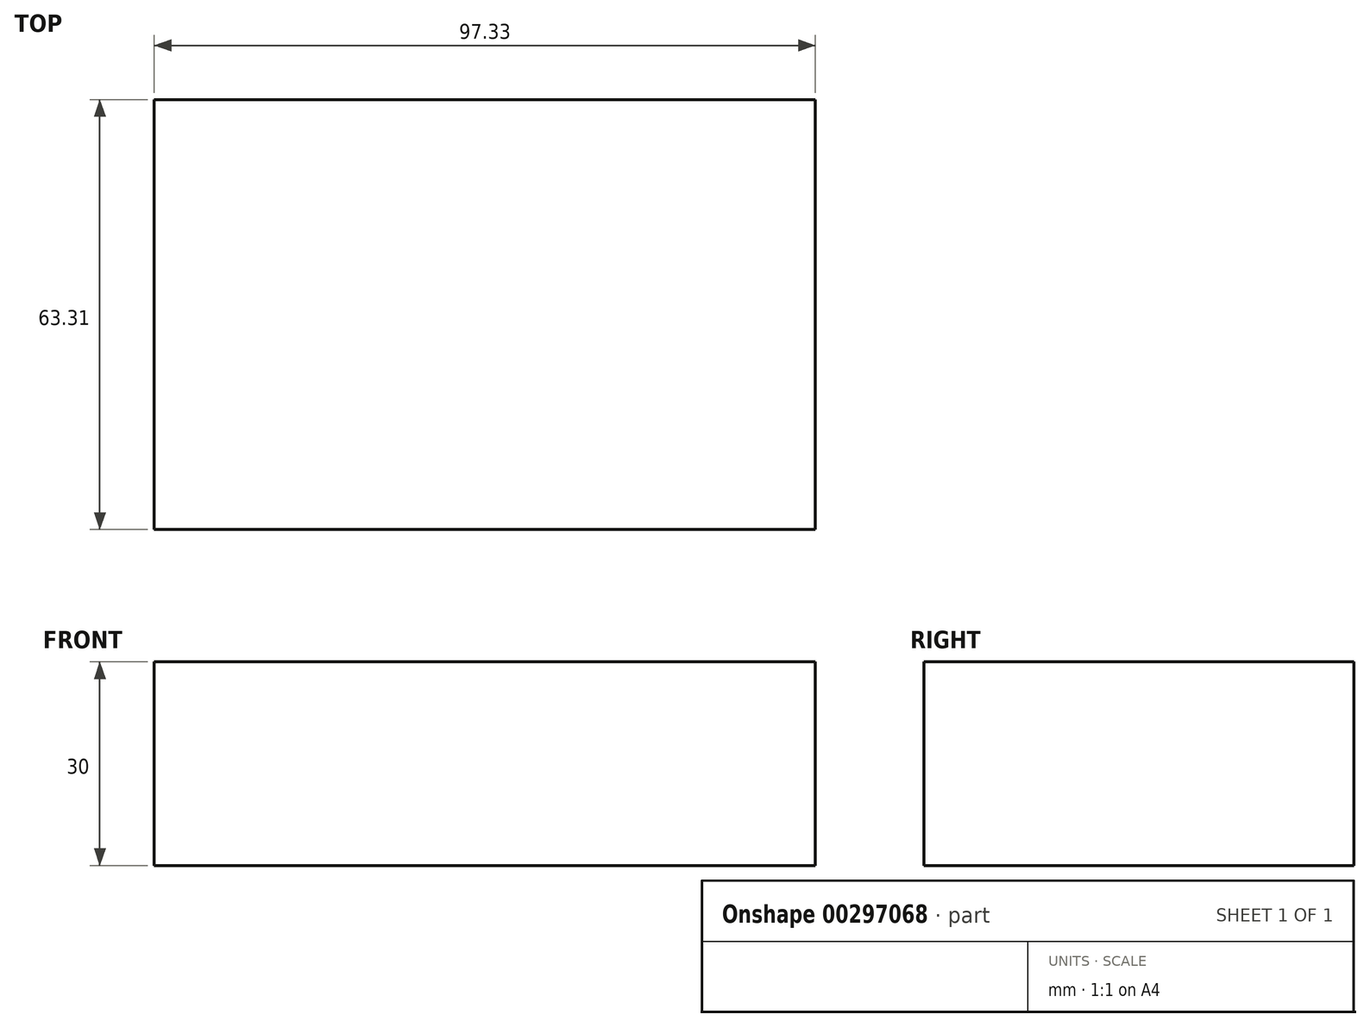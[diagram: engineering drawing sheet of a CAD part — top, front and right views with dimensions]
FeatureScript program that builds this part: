
annotation { "Feature Type Name" : "Feature", "Feature Type Description" : "" }
export const myFeature = defineFeature(function(context is Context, id is Id, definition is map)
    precondition{}
    {
        {
            var Q0;
            Q0=qCreatedBy(makeId("Top.planeOp"),FACE);
            var sketch = newSketch(context, id + "F0", { "sketchPlane" : qUnion([Q0])});
            skLineSegment(sketch, "E0.bottom", {"start": v(-44.73, 31.81) * mm, "end": v(52.6, 31.81) * mm});
            skLineSegment(sketch, "E0.top", {"start": v(-44.73, -31.5) * mm, "end": v(52.6, -31.5) * mm});
            skLineSegment(sketch, "E0.left", {"start": v(-44.73, 31.81) * mm, "end": v(-44.73, -31.5) * mm});
            skLineSegment(sketch, "E0.right", {"start": v(52.6, 31.81) * mm, "end": v(52.6, -31.5) * mm});
            skSolve(sketch);
        }
        {
            var Q0;
            Q0=makeQuery(id+"F0.imprint","IMPRINT",FACE,{"disambiguationData":[TD([[makeQuery(id+"F0.imprint","IMPRINT",EDGE,{"derivedFrom":sQuery(id+"F0.wireOp",EDGE,"E0.bottom")}),-1.0]])]});
            extrude(context, id + "F1", {"entities" : qUnion([Q0]), "depth" : 30 * mm});
        }
    });
